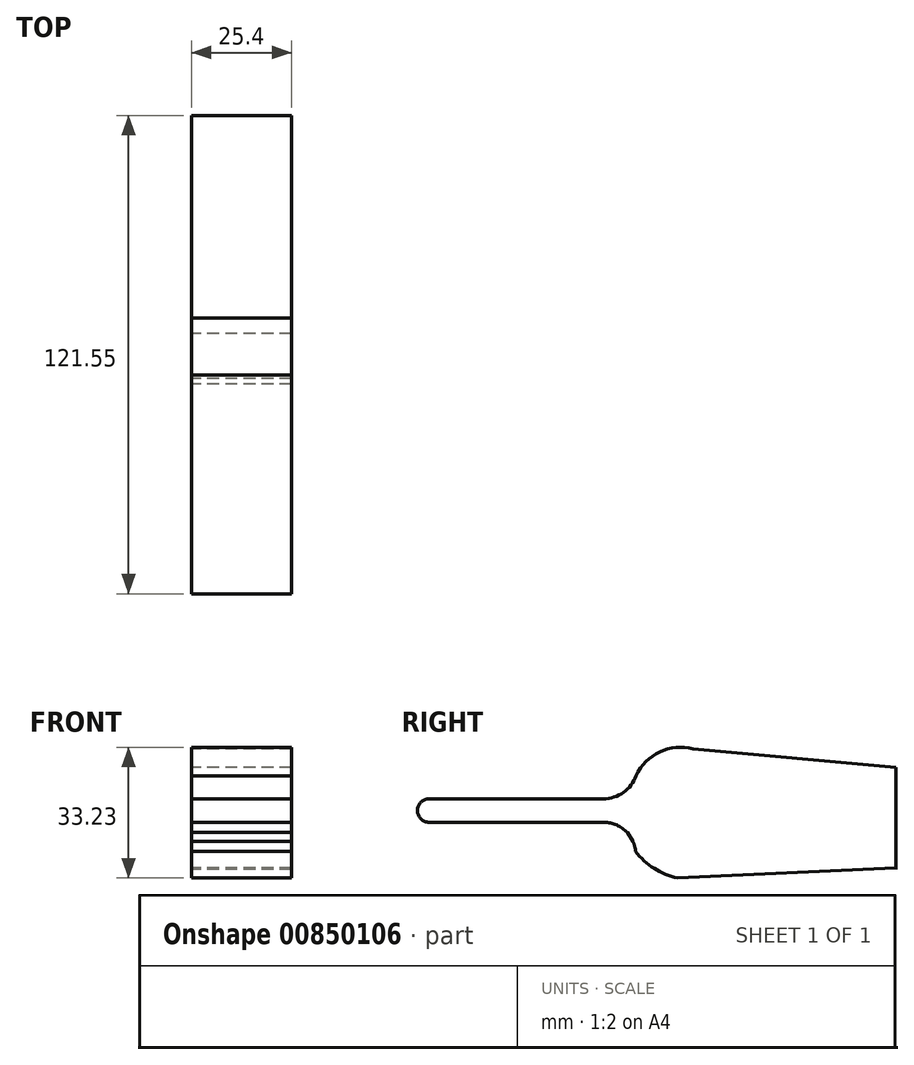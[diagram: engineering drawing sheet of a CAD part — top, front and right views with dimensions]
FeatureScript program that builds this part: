
annotation { "Feature Type Name" : "Feature", "Feature Type Description" : "" }
export const myFeature = defineFeature(function(context is Context, id is Id, definition is map)
    precondition{}
    {
        {
            var Q0;
            Q0=qCreatedBy(makeId("Right.planeOp"),FACE);
            var sketch = newSketch(context, id + "F0", { "sketchPlane" : qUnion([Q0])});
            skLineSegment(sketch, "E0", {"start": v(-12.42, 10.09) * mm, "end": v(-56.68, 10.09) * mm});
            skArc(sketch, "E1", {"start": v(-56.68, 10.09) * mm, "mid": v(-59.66, 7.1) * mm, "end": v(-56.68, 4.11) * mm});
            skLineSegment(sketch, "E2", {"start": v(-56.68, 4.11) * mm, "end": v(-12.27, 4.11) * mm});
            skArc(sketch, "E3", {"start": v(-12.42, 10.09) * mm, "mid": v(-7.33, 11.7) * mm, "end": v(-4.12, 15.97) * mm});
            skArc(sketch, "E4", {"start": v(-4.25, -3.28) * mm, "mid": v(-4.47, -1.94) * mm, "end": v(-4.91, -0.67) * mm});
            skLineSegment(sketch, "E5", {"start": v(-6.35, 1.52) * mm, "end": v(-4.91, -0.67) * mm});
            skArc(sketch, "E6", {"start": v(10.39, 22.78) * mm, "mid": v(1.91, 21.97) * mm, "end": v(-4.12, 15.97) * mm});
            skArc(sketch, "E7", {"start": v(-4.25, -3.28) * mm, "mid": v(0.5, -7.6) * mm, "end": v(6.42, -10.06) * mm});
            skLineSegment(sketch, "E8", {"start": v(10.39, 22.78) * mm, "end": v(61.9, 18.01) * mm});
            skLineSegment(sketch, "E9", {"start": v(61.9, 18.01) * mm, "end": v(61.9, -7.82) * mm});
            skLineSegment(sketch, "E10", {"start": v(61.9, -7.82) * mm, "end": v(61.9, -7.43) * mm});
            skLineSegment(sketch, "E11", {"start": v(61.9, -7.43) * mm, "end": v(6.42, -10.06) * mm});
            skArc(sketch, "E12", {"start": v(61.9, 18.01) * mm, "mid": v(64.54, 20.65) * mm, "end": v(67.16, 17.99) * mm});
            skLineSegment(sketch, "E13", {"start": v(67.16, 17.99) * mm, "end": v(67.16, -7.62) * mm});
            skArc(sketch, "E14", {"start": v(67.16, -7.62) * mm, "mid": v(64.43, -10.26) * mm, "end": v(61.9, -7.43) * mm});
            skPoint(sketch, "E15.orphan", {"position": v(-4.25, -4.6) * mm});
            skArc(sketch, "E16.trimOffspring", {"start": v(-6.35, 1.52) * mm, "mid": v(-9.04, 3.44) * mm, "end": v(-12.27, 4.11) * mm});
            skSolve(sketch);
        }
        {
            var Q0;
            {var subQ1=sQuery(id+"F0.wireOp",EDGE,"E12");var subQ2=sQuery(id+"F0.wireOp",EDGE,"E14");var subQ3=sQuery(id+"F0.wireOp",EDGE,"E9");var subQ4=makeQuery(id+"F0.imprint","INTERSECT",VERTEX,{"derivedFrom":[subQ3,subQ2]});var subQ7=makeQuery(id+"F0.imprint","IMPRINT",EDGE,{"disambiguationData":[TD([[subQ4,1.0]])],"derivedFrom":subQ3});Q0=qUnion([makeQuery(id+"F0.imprint","IMPRINT",FACE,{"disambiguationData":[TD([[makeQuery(id+"F0.imprint","IMPRINT",EDGE,{"derivedFrom":sQuery(id+"F0.wireOp",EDGE,"E0")}),1.0]])]}),makeQuery(id+"F0.imprint","IMPRINT",FACE,{"disambiguationData":[TD([[subQ7,-1.0]])]}),makeQuery(id+"F0.imprint","IMPRINT",FACE,{"disambiguationData":[TD([[makeQuery(id+"F0.imprint","IMPRINT",EDGE,{"derivedFrom":subQ1}),-1.0]])]})]);}
            extrude(context, id + "F1", {"entities" : qUnion([Q0]), "depth" : 25.4 * mm, "offsetDistance" : 25.4 * mm});
        }
    });
